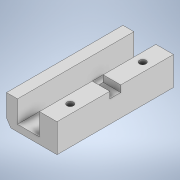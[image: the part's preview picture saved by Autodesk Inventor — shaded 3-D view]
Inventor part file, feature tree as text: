
AUTODESK INVENTOR PART (.ipt)
format: ipt  version: 2021 (Build 250183000, 183)  size: 153,600 bytes
history: native  units: mm
features: extrude x6, sketch x6, other x1
ambient origin geometry x8: Origin, YZ Plane, XZ Plane, XY Plane, X Axis, Y Axis, Z Axis, Center Point
bodies: Body1 (feature_tree)
feature tree (13):
  other  "Sólido1"
  extrude  "Extrusión1"  Depth=53.0mm
  extrude  "Extrusión2"  Depth=8.0mm
  extrude  "Extrusión3"  Depth=24.0mm
  extrude  "Extrusión4"  Depth=24.0mm
  extrude  "Extrusión5"  Depth=3.0mm
  extrude  "Extrusión7"  Depth=3.0mm
  sketch  "Boceto1"  dims[d0=23.0mm d1=53.0mm]
  sketch  "Boceto2"  dims[d2=3.0mm d3=0.0mm d4=8.0mm]
  sketch  "Boceto3"  dims[d5=10.0mm d6=0.0mm d7=24.0mm]
  sketch  "Boceto4"  dims[d8=5.0mm d9=24.0mm]
  sketch  "Boceto5"  dims[d10=3.0mm d11=0.0mm d12=3.0mm]
  sketch  "Boceto7"  dims[d13=10.0mm d14=4.0mm d15=14.75mm d16=0.0mm d17=5.0mm d18=10.0mm d19=0.0mm d24=2.0mm d25=3.0mm d26=55.5mm d27=0.0mm]
